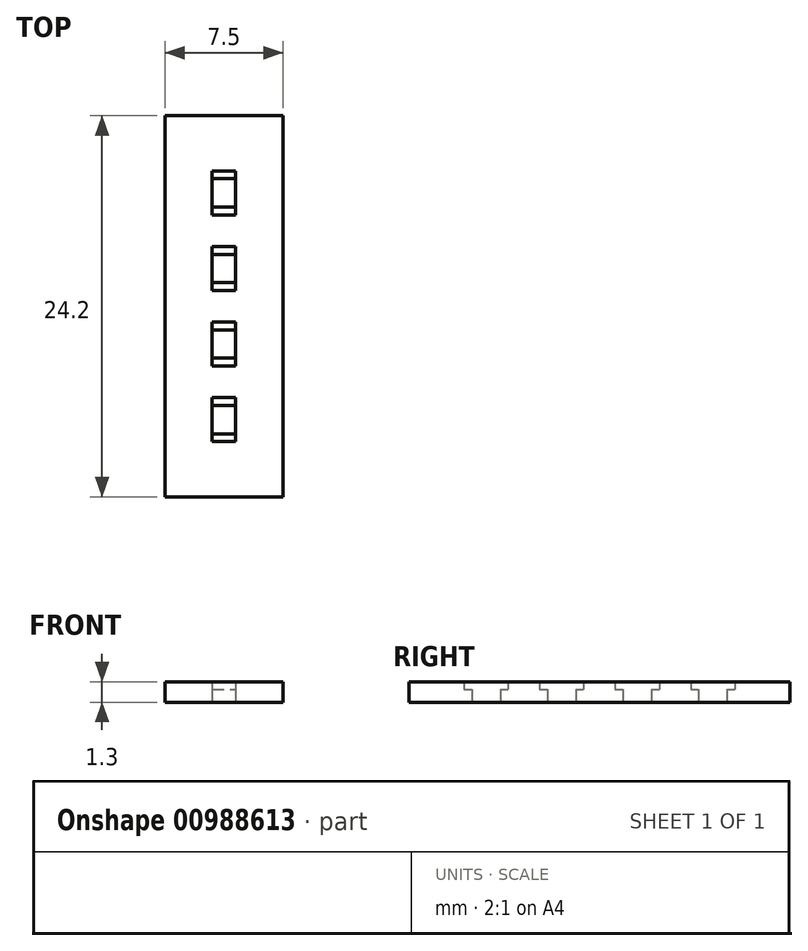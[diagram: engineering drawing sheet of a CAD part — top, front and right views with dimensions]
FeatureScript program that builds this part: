
annotation { "Feature Type Name" : "Feature", "Feature Type Description" : "" }
export const myFeature = defineFeature(function(context is Context, id is Id, definition is map)
    precondition{}
    {
        {
            var Q0;
            Q0=qCreatedBy(makeId("Top.planeOp"),FACE);
            var sketch = newSketch(context, id + "F0", { "sketchPlane" : qUnion([Q0])});
            skLineSegment(sketch, "E0.bottom", {"start": v(-27.6, 10.34) * mm, "end": v(-26.1, 10.34) * mm});
            skLineSegment(sketch, "E0.top", {"start": v(-27.6, 8.54) * mm, "end": v(-26.1, 8.54) * mm});
            skLineSegment(sketch, "E0.left", {"start": v(-27.6, 10.34) * mm, "end": v(-27.6, 8.54) * mm});
            skLineSegment(sketch, "E0.right", {"start": v(-26.1, 10.34) * mm, "end": v(-26.1, 8.54) * mm});
            skLineSegment(sketch, "E1.bottom", {"start": v(-27.6, 5.54) * mm, "end": v(-26.1, 5.54) * mm});
            skLineSegment(sketch, "E1.top", {"start": v(-27.6, 3.74) * mm, "end": v(-26.1, 3.74) * mm});
            skLineSegment(sketch, "E1.left", {"start": v(-27.6, 5.54) * mm, "end": v(-27.6, 3.74) * mm});
            skLineSegment(sketch, "E1.right", {"start": v(-26.1, 5.54) * mm, "end": v(-26.1, 3.74) * mm});
            skLineSegment(sketch, "E2.bottom", {"start": v(-27.6, 0.74) * mm, "end": v(-26.1, 0.74) * mm});
            skLineSegment(sketch, "E2.top", {"start": v(-27.6, -1.06) * mm, "end": v(-26.1, -1.06) * mm});
            skLineSegment(sketch, "E2.left", {"start": v(-27.6, 0.74) * mm, "end": v(-27.6, -1.06) * mm});
            skLineSegment(sketch, "E2.right", {"start": v(-26.1, 0.74) * mm, "end": v(-26.1, -1.06) * mm});
            skLineSegment(sketch, "E3.bottom", {"start": v(-27.6, -4.06) * mm, "end": v(-26.1, -4.06) * mm});
            skLineSegment(sketch, "E3.top", {"start": v(-27.6, -5.86) * mm, "end": v(-26.1, -5.86) * mm});
            skLineSegment(sketch, "E3.left", {"start": v(-27.6, -4.06) * mm, "end": v(-27.6, -5.86) * mm});
            skLineSegment(sketch, "E3.right", {"start": v(-26.1, -4.06) * mm, "end": v(-26.1, -5.86) * mm});
            skLineSegment(sketch, "E4.bottom", {"start": v(-30.6, 14.34) * mm, "end": v(-23.1, 14.34) * mm});
            skLineSegment(sketch, "E4.top", {"start": v(-30.6, -9.86) * mm, "end": v(-23.1, -9.86) * mm});
            skLineSegment(sketch, "E4.left", {"start": v(-30.6, 14.34) * mm, "end": v(-30.6, -9.86) * mm});
            skLineSegment(sketch, "E4.right", {"start": v(-23.1, 14.34) * mm, "end": v(-23.1, -9.86) * mm});
            skSolve(sketch);
        }
        {
            var Q0;
            Q0=makeQuery(id+"F0.imprint","IMPRINT",FACE,{"disambiguationData":[TD([[makeQuery(id+"F0.imprint","IMPRINT",EDGE,{"derivedFrom":sQuery(id+"F0.wireOp",EDGE,"E0.bottom")}),1.0]])]});
            extrude(context, id + "F1", {"entities" : qUnion([Q0]), "depth" : .8 * mm, "offsetDistance" : 25 * mm});
        }
        {
            var Q0;
            Q0=makeQuery(id+"F1.opExtrude","CAP_FACE",FACE,{"disambiguationData":[OSD([sQuery(id+"F0.wireOp",EDGE,"E0.bottom"),sQuery(id+"F0.wireOp",EDGE,"E0.top"),sQuery(id+"F0.wireOp",EDGE,"E0.left"),sQuery(id+"F0.wireOp",EDGE,"E0.right"),sQuery(id+"F0.wireOp",EDGE,"E1.bottom"),sQuery(id+"F0.wireOp",EDGE,"E1.top"),sQuery(id+"F0.wireOp",EDGE,"E1.left"),sQuery(id+"F0.wireOp",EDGE,"E1.right"),sQuery(id+"F0.wireOp",EDGE,"E2.bottom"),sQuery(id+"F0.wireOp",EDGE,"E2.top"),sQuery(id+"F0.wireOp",EDGE,"E2.left"),sQuery(id+"F0.wireOp",EDGE,"E2.right"),sQuery(id+"F0.wireOp",EDGE,"E3.bottom"),sQuery(id+"F0.wireOp",EDGE,"E3.top"),sQuery(id+"F0.wireOp",EDGE,"E3.left"),sQuery(id+"F0.wireOp",EDGE,"E3.right"),sQuery(id+"F0.wireOp",EDGE,"E4.bottom"),sQuery(id+"F0.wireOp",EDGE,"E4.top"),sQuery(id+"F0.wireOp",EDGE,"E4.left"),sQuery(id+"F0.wireOp",EDGE,"E4.right")])],"isStart":false});
            var sketch = newSketch(context, id + "F2", { "sketchPlane" : qUnion([Q0])});
            skLineSegment(sketch, "E5", {"start": v(-27.6, 8.04) * mm, "end": v(-26.1, 8.04) * mm});
            skLineSegment(sketch, "E6", {"start": v(-26.1, 8.04) * mm, "end": v(-26.1, 10.84) * mm});
            skLineSegment(sketch, "E7", {"start": v(-26.1, 10.84) * mm, "end": v(-27.6, 10.84) * mm});
            skLineSegment(sketch, "E8", {"start": v(-27.6, 10.84) * mm, "end": v(-27.6, 8.04) * mm});
            skLineSegment(sketch, "E9", {"start": v(-27.6, 6.04) * mm, "end": v(-26.1, 6.04) * mm});
            skLineSegment(sketch, "E10", {"start": v(-26.1, 6.04) * mm, "end": v(-26.1, 3.24) * mm});
            skLineSegment(sketch, "E11", {"start": v(-26.1, 3.24) * mm, "end": v(-27.6, 3.24) * mm});
            skLineSegment(sketch, "E12", {"start": v(-27.6, 3.24) * mm, "end": v(-27.6, 6.04) * mm});
            skLineSegment(sketch, "E13", {"start": v(-27.6, 1.24) * mm, "end": v(-26.1, 1.24) * mm});
            skLineSegment(sketch, "E14", {"start": v(-26.1, 1.24) * mm, "end": v(-26.1, -1.56) * mm});
            skLineSegment(sketch, "E15", {"start": v(-26.1, -1.56) * mm, "end": v(-27.6, -1.56) * mm});
            skLineSegment(sketch, "E16", {"start": v(-27.6, -1.56) * mm, "end": v(-27.6, 1.24) * mm});
            skLineSegment(sketch, "E17", {"start": v(-27.6, -3.56) * mm, "end": v(-26.1, -3.56) * mm});
            skLineSegment(sketch, "E18", {"start": v(-26.1, -3.56) * mm, "end": v(-26.1, -6.36) * mm});
            skLineSegment(sketch, "E19", {"start": v(-26.1, -6.36) * mm, "end": v(-27.6, -6.36) * mm});
            skLineSegment(sketch, "E20", {"start": v(-27.6, -6.36) * mm, "end": v(-27.6, -3.56) * mm});
            skLineSegment(sketch, "E21.bottom", {"start": v(-30.6, 14.34) * mm, "end": v(-23.1, 14.34) * mm});
            skLineSegment(sketch, "E21.top", {"start": v(-30.6, -9.86) * mm, "end": v(-23.1, -9.86) * mm});
            skLineSegment(sketch, "E21.left", {"start": v(-30.6, 14.34) * mm, "end": v(-30.6, -9.86) * mm});
            skLineSegment(sketch, "E21.right", {"start": v(-23.1, 14.34) * mm, "end": v(-23.1, -9.86) * mm});
            skSolve(sketch);
        }
        {
            var Q0;
            {var subQ26=sQuery(id+"F2.wireOp",EDGE,"E5");Q0=makeQuery(id+"F2.imprint","IMPRINT",FACE,{"disambiguationData":[TD([[makeQuery(id+"F2.imprint","IMPRINT",EDGE,{"derivedFrom":subQ26}),-1.0]])]});}
            extrude(context, id + "F3", {"entities" : qUnion([Q0]), "operationType" : NewBodyOperationType.ADD, "depth" : .5 * mm, "offsetDistance" : 25 * mm});
        }
    });
